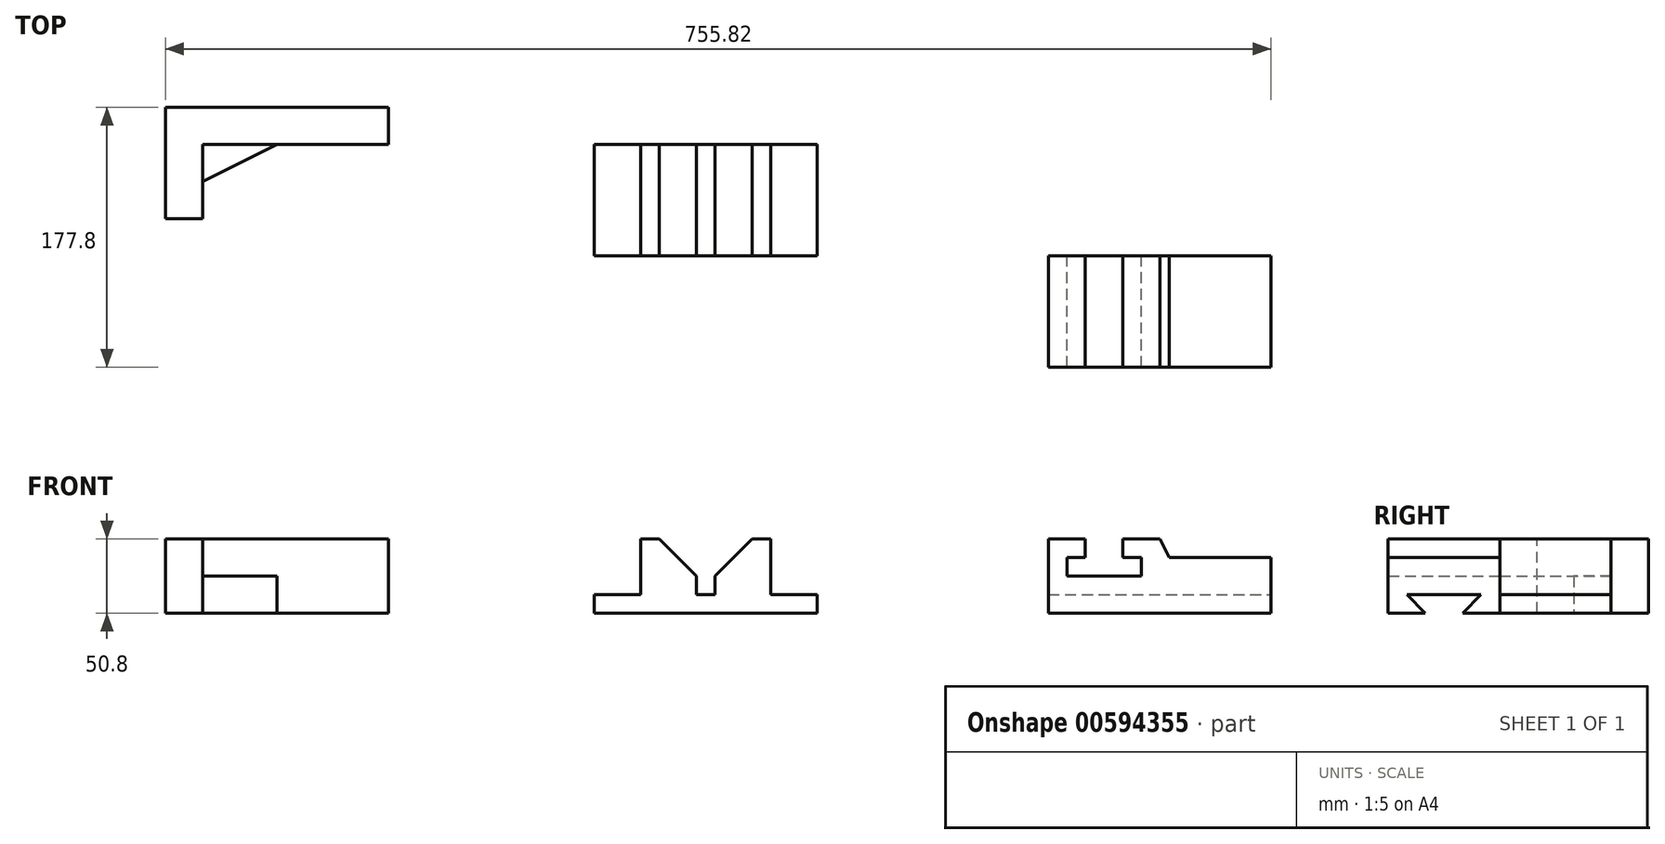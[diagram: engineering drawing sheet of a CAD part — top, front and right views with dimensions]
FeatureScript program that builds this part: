
annotation { "Feature Type Name" : "Feature", "Feature Type Description" : "" }
export const myFeature = defineFeature(function(context is Context, id is Id, definition is map)
    precondition{}
    {
        {
            var Q0;
            Q0=qCreatedBy(makeId("Front.planeOp"),FACE);
            var sketch = newSketch(context, id + "F0", { "sketchPlane" : qUnion([Q0])});
            skLineSegment(sketch, "E0.bottom", {"start": v(0, 0) * mm, "end": v(25.4, 0) * mm});
            skLineSegment(sketch, "E0.top", {"start": v(0, 50.8) * mm, "end": v(25.4, 50.8) * mm});
            skLineSegment(sketch, "E0.left", {"start": v(0, 0) * mm, "end": v(0, 50.8) * mm});
            skLineSegment(sketch, "E0.right", {"start": v(25.4, 0) * mm, "end": v(25.4, 50.8) * mm});
            skSolve(sketch);
        }
        {
            var Q0;
            Q0=makeQuery(id+"F0.imprint","IMPRINT",FACE,{"disambiguationData":[TD([[makeQuery(id+"F0.imprint","IMPRINT",EDGE,{"derivedFrom":sQuery(id+"F0.wireOp",EDGE,"E0.bottom")}),1.0]])]});
            extrude(context, id + "F1", {"entities" : qUnion([Q0]), "depth" : 76.2 * mm, "offsetDistance" : 25.4 * mm});
        }
        {
            var Q0;
            Q0=makeQuery(id+"F1.opExtrude","CAP_FACE",FACE,{"disambiguationData":[OSD([sQuery(id+"F0.wireOp",EDGE,"E0.bottom"),sQuery(id+"F0.wireOp",EDGE,"E0.top"),sQuery(id+"F0.wireOp",EDGE,"E0.left"),sQuery(id+"F0.wireOp",EDGE,"E0.right")])],"isStart":true});
            var sketch = newSketch(context, id + "F2", { "sketchPlane" : qUnion([Q0])});
            skLineSegment(sketch, "E1.bottom", {"start": v(0, 50.8) * mm, "end": v(-152.4, 50.8) * mm});
            skLineSegment(sketch, "E1.top", {"start": v(0, 0) * mm, "end": v(-152.4, 0) * mm});
            skLineSegment(sketch, "E1.left", {"start": v(0, 50.8) * mm, "end": v(0, 0) * mm});
            skLineSegment(sketch, "E1.right", {"start": v(-152.4, 50.8) * mm, "end": v(-152.4, 0) * mm});
            skSolve(sketch);
        }
        {
            var Q0;
            {var subQ2=sQuery(id+"F2.wireOp",EDGE,"E1.right");Q0=makeQuery(id+"F2.imprint","IMPRINT",FACE,{"disambiguationData":[TD([[makeQuery(id+"F2.imprint","IMPRINT",EDGE,{"derivedFrom":subQ2}),1.0]])]});}
            var Q1;
            {var subQ0=sQuery(id+"F2.wireOp",EDGE,"E1.left");Q1=makeQuery(id+"F2.imprint","IMPRINT",FACE,{"disambiguationData":[TD([[makeQuery(id+"F2.imprint","IMPRINT",EDGE,{"derivedFrom":subQ0}),1.0]])]});}
            extrude(context, id + "F3", {"entities" : qUnion([Q0, Q1]), "operationType" : NewBodyOperationType.ADD, "oppositeDirection" : true, "depth" : 25.4 * mm, "offsetDistance" : 25.4 * mm});
        }
        {
            var Q0;
            Q0=qCreatedBy(makeId("Top.planeOp"),FACE);
            var sketch = newSketch(context, id + "F4", { "sketchPlane" : qUnion([Q0])});
            skLineSegment(sketch, "E2", {"start": v(25.4, -25.4) * mm, "end": v(76.2, -25.4) * mm});
            skLineSegment(sketch, "E3", {"start": v(25.4, -25.4) * mm, "end": v(25.4, -50.8) * mm});
            skLineSegment(sketch, "E4", {"start": v(76.2, -25.4) * mm, "end": v(25.4, -50.8) * mm});
            skSolve(sketch);
        }
        {
            var Q0;
            Q0=makeQuery(id+"F4.imprint","IMPRINT",FACE,{"disambiguationData":[TD([[makeQuery(id+"F4.imprint","IMPRINT",EDGE,{"derivedFrom":sQuery(id+"F4.wireOp",EDGE,"E2")}),-1.0]])]});
            extrude(context, id + "F5", {"entities" : qUnion([Q0]), "operationType" : NewBodyOperationType.ADD, "depth" : 25.4 * mm, "offsetDistance" : 25.4 * mm});
        }
        {
            var Q0;
            Q0=makeQuery(id+"F3.opExtrude","CAP_FACE",FACE,{"disambiguationData":[OSD([sQuery(id+"F2.wireOp",EDGE,"E1.bottom"),sQuery(id+"F2.wireOp",EDGE,"E1.top"),sQuery(id+"F2.wireOp",EDGE,"E1.left"),sQuery(id+"F2.wireOp",EDGE,"E1.right")])],"isStart":false});
            var sketch = newSketch(context, id + "F6", { "sketchPlane" : qUnion([Q0])});
            skLineSegment(sketch, "E5", {"start": v(293.15, 0) * mm, "end": v(445.55, 0) * mm});
            skLineSegment(sketch, "E6", {"start": v(293.15, 0) * mm, "end": v(293.15, 12.7) * mm});
            skLineSegment(sketch, "E7", {"start": v(445.55, 0) * mm, "end": v(445.55, 12.7) * mm});
            skLineSegment(sketch, "E8", {"start": v(293.15, 12.7) * mm, "end": v(324.9, 12.7) * mm});
            skLineSegment(sketch, "E9", {"start": v(445.55, 12.7) * mm, "end": v(413.8, 12.7) * mm});
            skLineSegment(sketch, "E10", {"start": v(324.9, 12.7) * mm, "end": v(324.9, 50.8) * mm});
            skLineSegment(sketch, "E11", {"start": v(413.8, 12.7) * mm, "end": v(413.8, 50.8) * mm});
            skLineSegment(sketch, "E12", {"start": v(324.9, 50.8) * mm, "end": v(337.6, 50.8) * mm});
            skLineSegment(sketch, "E13", {"start": v(413.8, 50.8) * mm, "end": v(401.1, 50.8) * mm});
            skLineSegment(sketch, "E14", {"start": v(363, 12.7) * mm, "end": v(363, 25.4) * mm});
            skLineSegment(sketch, "E15", {"start": v(375.7, 12.7) * mm, "end": v(375.7, 25.4) * mm});
            skLineSegment(sketch, "E16", {"start": v(363, 12.7) * mm, "end": v(375.7, 12.7) * mm});
            skLineSegment(sketch, "E17", {"start": v(337.6, 50.8) * mm, "end": v(363, 25.4) * mm});
            skLineSegment(sketch, "E18", {"start": v(401.1, 50.8) * mm, "end": v(375.7, 25.4) * mm});
            skSolve(sketch);
        }
        {
            var Q0;
            Q0=makeQuery(id+"F6.imprint","IMPRINT",FACE,{"disambiguationData":[TD([[makeQuery(id+"F6.imprint","IMPRINT",EDGE,{"derivedFrom":sQuery(id+"F6.wireOp",EDGE,"E5")}),1.0]])]});
            extrude(context, id + "F7", {"entities" : qUnion([Q0]), "depth" : 76.2 * mm, "offsetDistance" : 25.4 * mm});
        }
        {
            var Q0;
            Q0=makeQuery(id+"F7.opExtrude","CAP_FACE",FACE,{"disambiguationData":[OSD([sQuery(id+"F6.wireOp",EDGE,"E5"),sQuery(id+"F6.wireOp",EDGE,"E6"),sQuery(id+"F6.wireOp",EDGE,"E7"),sQuery(id+"F6.wireOp",EDGE,"E8"),sQuery(id+"F6.wireOp",EDGE,"E9"),sQuery(id+"F6.wireOp",EDGE,"E10"),sQuery(id+"F6.wireOp",EDGE,"E11"),sQuery(id+"F6.wireOp",EDGE,"E12"),sQuery(id+"F6.wireOp",EDGE,"E13"),sQuery(id+"F6.wireOp",EDGE,"E14"),sQuery(id+"F6.wireOp",EDGE,"E15"),sQuery(id+"F6.wireOp",EDGE,"E16"),sQuery(id+"F6.wireOp",EDGE,"E17"),sQuery(id+"F6.wireOp",EDGE,"E18")])],"isStart":false});
            var sketch = newSketch(context, id + "F8", { "sketchPlane" : qUnion([Q0])});
            skLineSegment(sketch, "E19", {"start": v(603.42, 0) * mm, "end": v(755.82, 0) * mm});
            skLineSegment(sketch, "E20", {"start": v(755.82, 0) * mm, "end": v(755.82, 38.1) * mm});
            skLineSegment(sketch, "E21", {"start": v(603.42, 0) * mm, "end": v(603.42, 50.8) * mm});
            skLineSegment(sketch, "E22", {"start": v(603.42, 50.8) * mm, "end": v(628.82, 50.8) * mm});
            skLineSegment(sketch, "E23", {"start": v(628.82, 50.8) * mm, "end": v(628.82, 38.1) * mm});
            skLineSegment(sketch, "E24", {"start": v(628.82, 38.1) * mm, "end": v(616.12, 38.1) * mm});
            skLineSegment(sketch, "E25", {"start": v(616.12, 38.1) * mm, "end": v(616.12, 25.4) * mm});
            skLineSegment(sketch, "E26", {"start": v(616.12, 25.4) * mm, "end": v(666.92, 25.4) * mm});
            skLineSegment(sketch, "E27", {"start": v(666.92, 25.4) * mm, "end": v(666.92, 38.1) * mm});
            skLineSegment(sketch, "E28", {"start": v(666.92, 38.1) * mm, "end": v(654.22, 38.1) * mm});
            skLineSegment(sketch, "E29", {"start": v(654.22, 38.1) * mm, "end": v(654.22, 50.8) * mm});
            skLineSegment(sketch, "E30", {"start": v(654.22, 50.8) * mm, "end": v(679.62, 50.8) * mm});
            skLineSegment(sketch, "E31", {"start": v(755.82, 38.1) * mm, "end": v(685.97, 38.1) * mm});
            skLineSegment(sketch, "E32", {"start": v(679.62, 50.8) * mm, "end": v(685.97, 38.1) * mm});
            skSolve(sketch);
        }
        {
            var Q0;
            Q0=makeQuery(id+"F8.imprint","IMPRINT",FACE,{"disambiguationData":[TD([[makeQuery(id+"F8.imprint","IMPRINT",EDGE,{"derivedFrom":sQuery(id+"F8.wireOp",EDGE,"E19")}),1.0]])]});
            extrude(context, id + "F9", {"entities" : qUnion([Q0]), "depth" : 76.2 * mm, "offsetDistance" : 25.4 * mm});
        }
        {
            var Q0;
            Q0=makeQuery(id+"F9.opExtrude","SWEPT_FACE",FACE,{"disambiguationData":[OSD([sQuery(id+"F8.wireOp",EDGE,"E20")])]});
            var sketch = newSketch(context, id + "F10", { "sketchPlane" : qUnion([Q0])});
            skLineSegment(sketch, "E33", {"start": v(-177.8, 0) * mm, "end": v(-152.4, 0) * mm});
            skLineSegment(sketch, "E34", {"start": v(-101.6, 0) * mm, "end": v(-127, 0) * mm});
            skLineSegment(sketch, "E35", {"start": v(-139.7, 12.7) * mm, "end": v(-165.1, 12.7) * mm});
            skLineSegment(sketch, "E36", {"start": v(-139.7, 12.7) * mm, "end": v(-114.3, 12.7) * mm});
            skLineSegment(sketch, "E37", {"start": v(-165.1, 12.7) * mm, "end": v(-152.4, 0) * mm});
            skLineSegment(sketch, "E38", {"start": v(-114.3, 12.7) * mm, "end": v(-127, 0) * mm});
            skSolve(sketch);
        }
        {
            var Q0;
            Q0=makeQuery(id+"F10.imprint","IMPRINT",FACE,{"disambiguationData":[TD([[makeQuery(id+"F10.imprint","IMPRINT",EDGE,{"derivedFrom":sQuery(id+"F10.wireOp",EDGE,"E35")}),1.0]])]});
            extrude(context, id + "F11", {"entities" : qUnion([Q0]), "operationType" : NewBodyOperationType.REMOVE, "oppositeDirection" : true, "depth" : 152.4 * mm, "offsetDistance" : 25.4 * mm});
        }
    });
